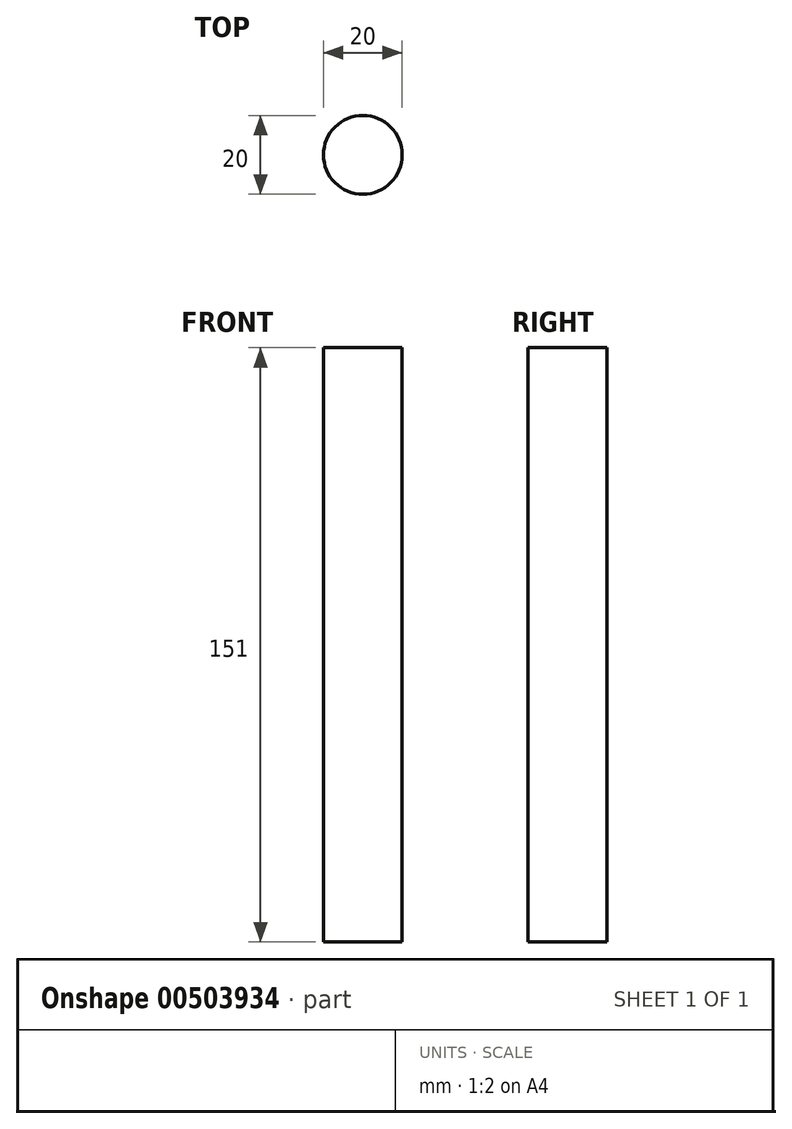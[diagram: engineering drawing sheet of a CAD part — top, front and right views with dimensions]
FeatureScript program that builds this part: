
annotation { "Feature Type Name" : "Feature", "Feature Type Description" : "" }
export const myFeature = defineFeature(function(context is Context, id is Id, definition is map)
    precondition{}
    {
        {
            var Q0;
            Q0=qCreatedBy(makeId("Top.planeOp"),FACE);
            var sketch = newSketch(context, id + "F0", { "sketchPlane" : qUnion([Q0])});
            skCircle(sketch, "E0", {"center": v(0, 0) * mm, "radius": 10 * mm});
            skSolve(sketch);
        }
        {
            var Q0;
            Q0=makeQuery(id+"F0.imprint","IMPRINT",FACE,{"disambiguationData":[TD([[makeQuery(id+"F0.imprint","IMPRINT",EDGE,{"derivedFrom":sQuery(id+"F0.wireOp",EDGE,"E0")}),1.0]])]});
            var Q1;
            Q1=sQuery(id+"F0.wireOp",EDGE,"E0");
            extrude(context, id + "F1", {"entities" : qUnion([Q0]), "surfaceEntities" : qUnion([Q1]), "depth" : 100 * mm, "hasSecondDirection" : true, "secondDirectionOppositeDirection" : true, "secondDirectionDepth" : 51 * mm});
        }
    });
